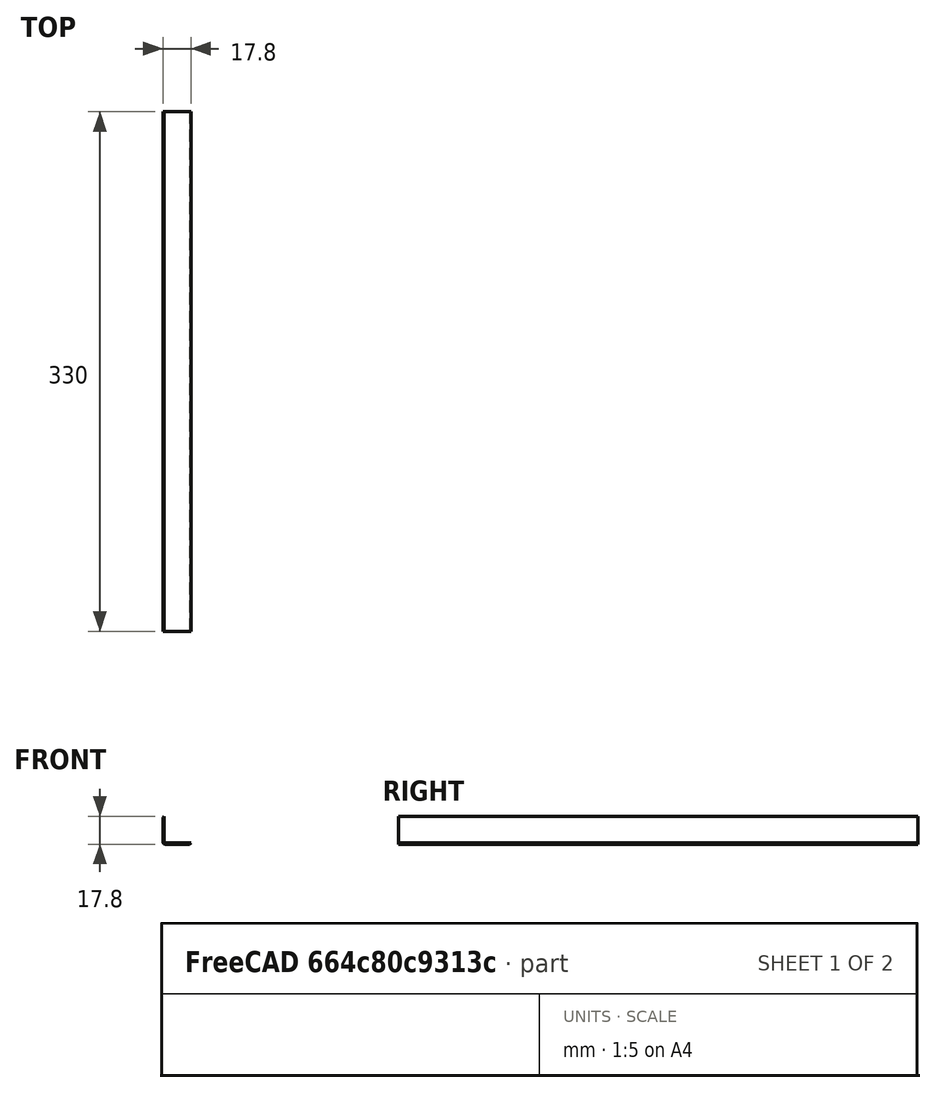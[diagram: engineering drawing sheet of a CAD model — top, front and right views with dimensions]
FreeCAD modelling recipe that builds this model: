
FCSTD DOCUMENT  (FreeCAD 0.19R23463 (Git))
Label: KallaxEdgeProtector
License: All rights reserved
LicenseURL: http://en.wikipedia.org/wiki/All_rights_reserved
objects: Sketcher::SketchObject×1, PartDesign::Pad×1, PartDesign::Body×1
note: 4 computed .brp shape members not serialized (recipe doc carries the construction recipe); baked Part::Feature solids carry a one-line shape summary decoded from their .brp

FEATURE [Sketcher::SketchObject] Sketch
  MapMode = 5
  Placement = pos=(0,0,0) rot=(1,0,0;1.5708rad)
  Support = -> [XZ_Plane]
  sketch-geometry (8):
    g0: LineSegment StartX=-9.3 StartY=7.7 StartZ=0 EndX=-9.3 EndY=-7.7 EndZ=0
    g1: LineSegment StartX=-7.7 StartY=-9.3 StartZ=0 EndX=7.7 EndY=-9.3 EndZ=0
    g2: LineSegment StartX=7.7 StartY=-9.3 StartZ=0 EndX=8.5 EndY=-8.5 EndZ=0
    g3: LineSegment StartX=8.5 StartY=-8.5 StartZ=0 EndX=-7.7 EndY=-8.5 EndZ=0
    g4: LineSegment StartX=-8.5 StartY=-7.7 StartZ=0 EndX=-8.5 EndY=8.5 EndZ=0
    g5: LineSegment StartX=-8.5 StartY=8.5 StartZ=0 EndX=-9.3 EndY=7.7 EndZ=0
    g6: ArcOfCircle CenterX=-7.7 CenterY=-7.7 CenterZ=0 NormalX=0 NormalY=0 NormalZ=1 AngleXU=0 Radius=0.8 StartAngle=3.14159 EndAngle=4.71239
    g7: ArcOfCircle CenterX=-7.7 CenterY=-7.7 CenterZ=0 NormalX=0 NormalY=0 NormalZ=1 AngleXU=0 Radius=1.6 StartAngle=3.14159 EndAngle=4.71239
  constraints (20):
    c: Vertical(g0)
    c: Horizontal(g1)
    c: Coincident(g1,g2)
    c: Coincident(g2,g3)
    c: Horizontal(g3)
    c: Coincident(g4,g5)
    c: Coincident(g5,g0)
    c: Equal(g3,g4)
    c: DistanceX(g4,g2) = 17
    c: Equal(g2,g5)
    c: DistanceX(g5,g5) = 0.8
    c: Tangent(g3,g6) = 1.5708
    c: Tangent(g4,g6) = 1.5708
    c: Tangent(g0,g7) = -1.5708
    c: Tangent(g1,g7) = -1.5708
    c: Coincident(g6,g7)
    c: Radius(g6) = 0.8
    c: Angle(g5,g4) = 0.785398
    c: Equal(g1,g0)
    c: Symmetric(g4,g2,g-1)
FEATURE [PartDesign::Pad] Pad
  Direction = (1,1,1)
  Length = 330
  Length2 = 100
  Placement = pos=(0,0,0) rot=(1,0,0;1.5708rad)
  Profile = -> Sketch
  Type = 0
FEATURE [PartDesign::Body] Body
  Group = -> [Sketch,Pad]
  Origin = -> Origin
  Tip = -> Pad
